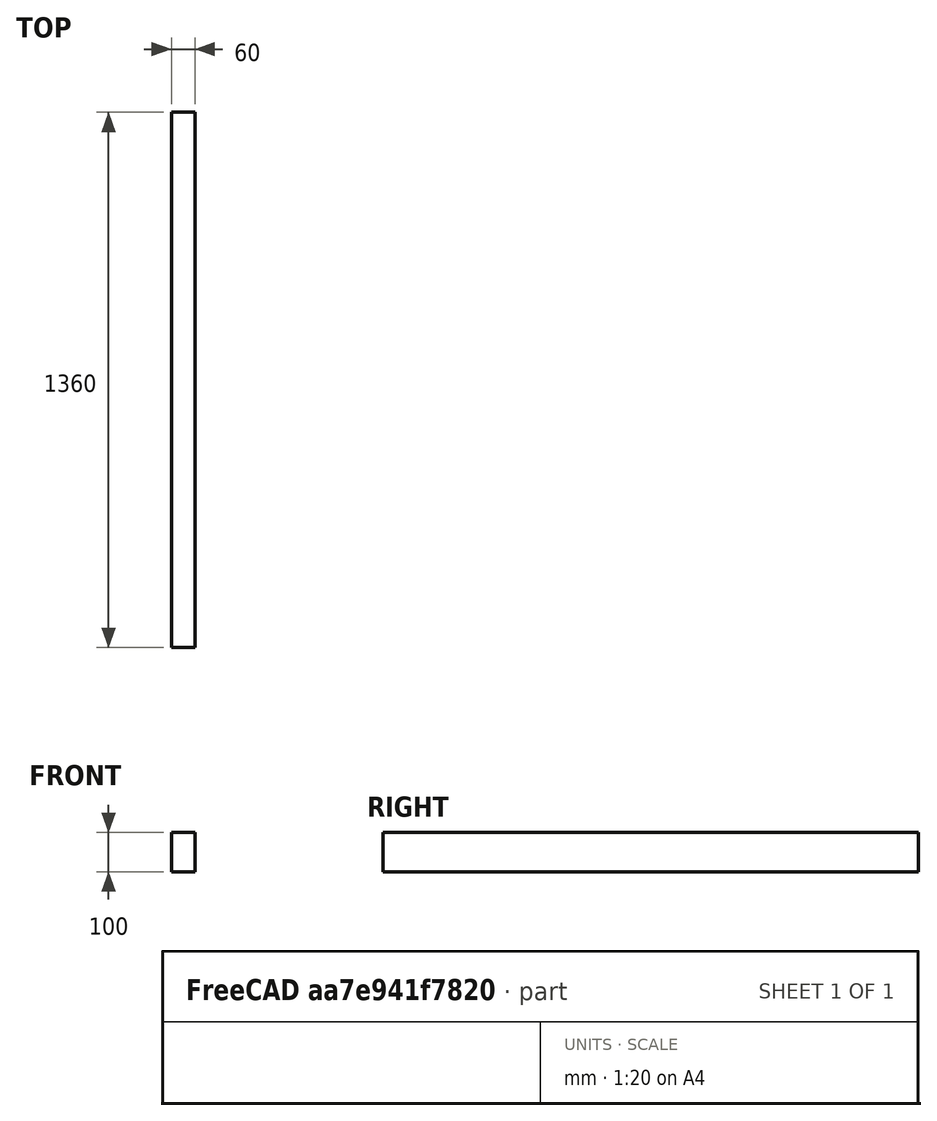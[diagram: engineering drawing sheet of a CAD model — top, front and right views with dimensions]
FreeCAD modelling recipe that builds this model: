
FCSTD DOCUMENT  (FreeCAD 1.0RUnknown)
Label: beam60x100x1500
License: All rights reserved
LicenseURL: https://en.wikipedia.org/wiki/All_rights_reserved
objects: PartDesign::CoordinateSystem×3, Sketcher::SketchObject×1, PartDesign::Pad×1, PartDesign::Body×1, App::Part×1
note: 9 computed .brp shape members not serialized (recipe doc carries the construction recipe); baked Part::Feature solids carry a one-line shape summary decoded from their .brp

FEATURE [Sketcher::SketchObject] Sketch
  ArcFitTolerance = 1e-06
  AttachmentSupport = -> [XZ_Plane]
  FullyConstrained = true
  MakeInternals = false
  MapMode = 5
  Placement = pos=(0,0,0) rot=(1,0,0;1.5708rad)
  sketch-geometry (5):
    g0: LineSegment StartX=-30 StartY=-50 StartZ=0 EndX=30 EndY=-50 EndZ=0
    g1: LineSegment StartX=30 StartY=-50 StartZ=0 EndX=30 EndY=50 EndZ=0
    g2: LineSegment StartX=30 StartY=50 StartZ=0 EndX=-30 EndY=50 EndZ=0
    g3: LineSegment StartX=-30 StartY=50 StartZ=0 EndX=-30 EndY=-50 EndZ=0
    g4: GeomPoint [constr] X=0 Y=0 Z=0
  constraints (12):
    c: Coincident(g0,g1)
    c: Coincident(g1,g2)
    c: Coincident(g2,g3)
    c: Coincident(g3,g0)
    c: Horizontal(g0)
    c: Horizontal(g2)
    c: Vertical(g1)
    c: Vertical(g3)
    c: Symmetric(g2,g0,g4)
    c: Coincident(g4,g-1)
    c: DistanceX(g0,g0) = 60
    c: DistanceY(g3,g3) = 100
FEATURE [PartDesign::Pad] Pad
  Direction = (0,-1,2e-16)
  Length = 1360
  Length2 = 10
  Midplane = true
  Placement = pos=(0,0,0) rot=(1,0,0;1.5708rad)
  Profile = -> Sketch
  ReferenceAxis = -> Sketch [N_Axis]
  Refine = true
  Suppressed = false
  Type = 0
FEATURE [PartDesign::Body] Body  label="Körper"
  AllowCompound = false
  Group = -> [Sketch,Pad]
  Origin = -> Origin
  Tip = -> Pad
FEATURE [PartDesign::CoordinateSystem] LCS_Origin
  AttacherType = Attacher::AttachEngine3D
  AttachmentSupport = -> [X_Axis001]
  MapMode = 2
FEATURE [PartDesign::CoordinateSystem] LCS_1
  AttacherType = Attacher::AttachEngine3D
  AttachmentSupport = -> [Pad]
  MapMode = 45
  Placement = pos=(-30,680,-1.51e-13) rot=(0,0,1;0rad)
FEATURE [PartDesign::CoordinateSystem] LCS_2
  AttacherType = Attacher::AttachEngine3D
  AttachmentSupport = -> [Pad]
  MapMode = 45
  Placement = pos=(-30,-680,1.51e-13) rot=(0,0,1;0rad)
FEATURE [App::Part] beam60x100x887  label="beam60x100x800"
  Group = -> [LCS_Origin,Body,LCS_1,LCS_2]
  Origin = -> Origin001
